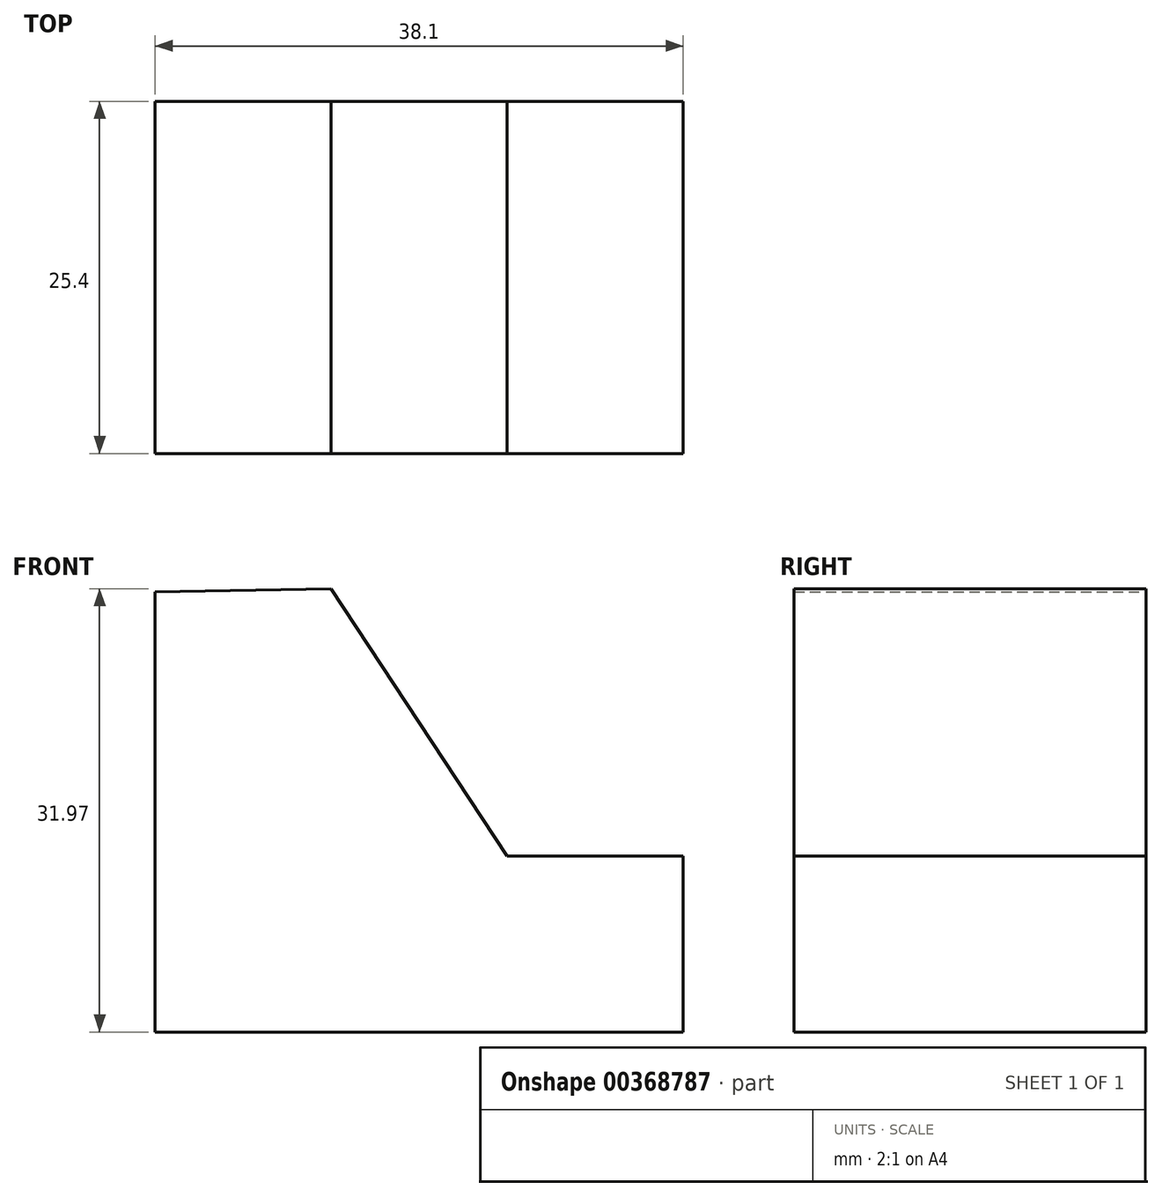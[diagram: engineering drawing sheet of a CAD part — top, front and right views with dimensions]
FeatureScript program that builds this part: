
annotation { "Feature Type Name" : "Feature", "Feature Type Description" : "" }
export const myFeature = defineFeature(function(context is Context, id is Id, definition is map)
    precondition{}
    {
        {
            var Q0;
            Q0=qCreatedBy(makeId("Front.planeOp"),FACE);
            var sketch = newSketch(context, id + "F0", { "sketchPlane" : qUnion([Q0])});
            skLineSegment(sketch, "E0", {"start": v(0, 31.75) * mm, "end": v(0, 0) * mm});
            skLineSegment(sketch, "E1", {"start": v(0, 0) * mm, "end": v(38.1, 0) * mm});
            skLineSegment(sketch, "E2", {"start": v(38.1, 0) * mm, "end": v(38.1, 12.7) * mm});
            skLineSegment(sketch, "E3", {"start": v(38.1, 12.7) * mm, "end": v(25.4, 12.7) * mm});
            skLineSegment(sketch, "E4", {"start": v(25.4, 12.7) * mm, "end": v(12.7, 31.97) * mm});
            skLineSegment(sketch, "E5", {"start": v(12.7, 31.97) * mm, "end": v(0, 31.75) * mm});
            skSolve(sketch);
        }
        {
            var Q0;
            Q0=makeQuery(id+"F0.imprint","IMPRINT",FACE,{"disambiguationData":[TD([[makeQuery(id+"F0.imprint","IMPRINT",EDGE,{"derivedFrom":sQuery(id+"F0.wireOp",EDGE,"E0")}),1.0]])]});
            extrude(context, id + "F1", {"entities" : qUnion([Q0]), "depth" : 25.4 * mm});
        }
    });
